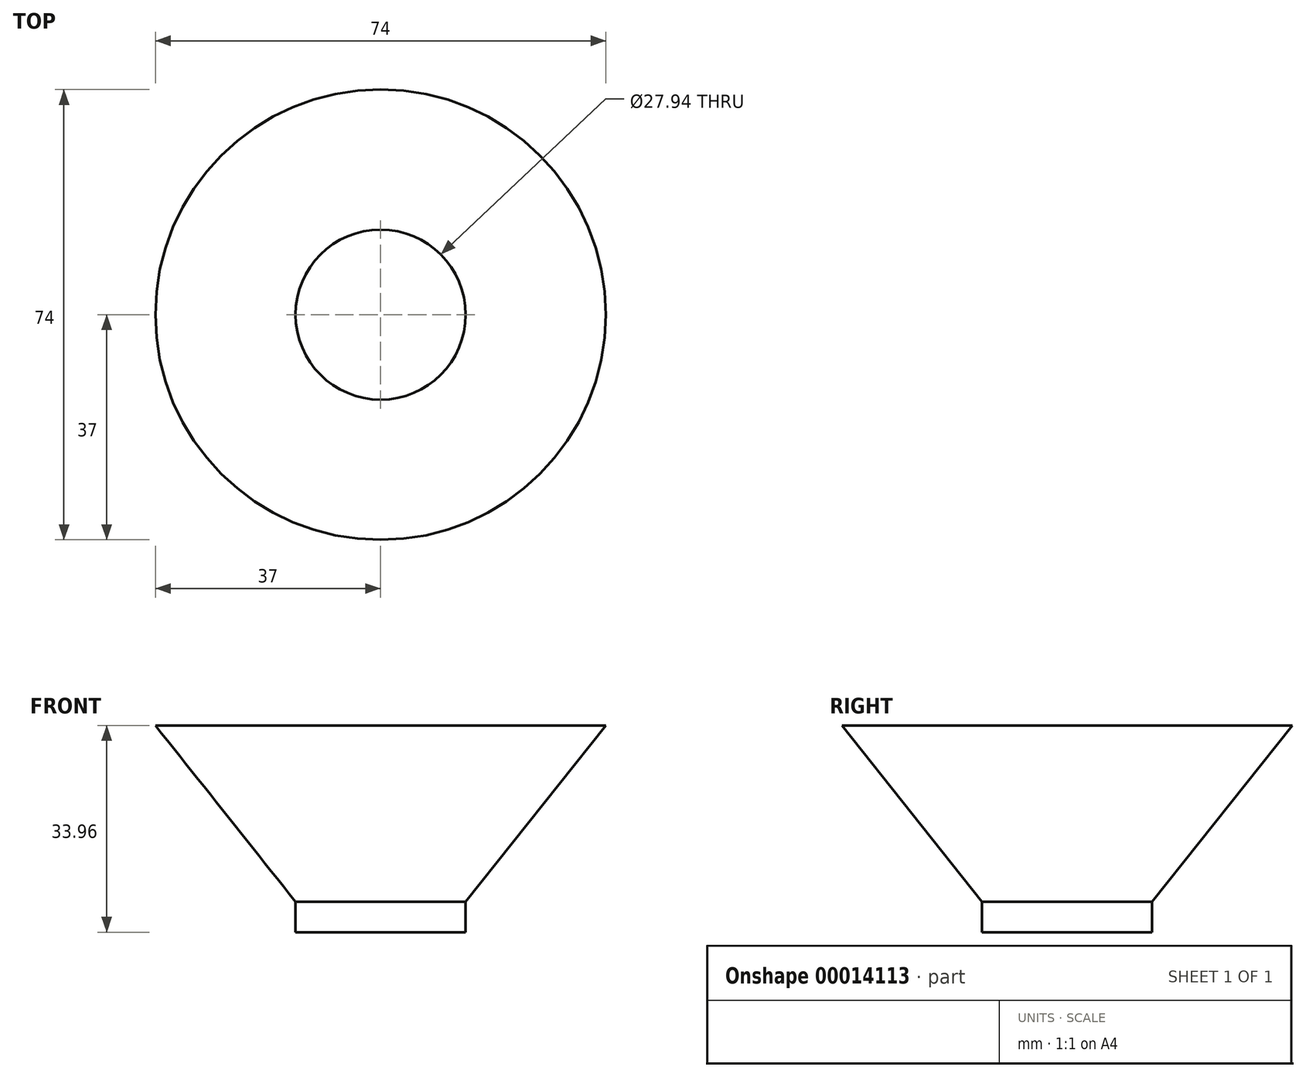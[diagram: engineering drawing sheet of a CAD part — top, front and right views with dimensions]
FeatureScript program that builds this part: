
annotation { "Feature Type Name" : "Feature", "Feature Type Description" : "" }
export const myFeature = defineFeature(function(context is Context, id is Id, definition is map)
    precondition{}
    {
        {
            var Q0;
            Q0=qCreatedBy(makeId("Front.planeOp"),FACE);
            var sketch = newSketch(context, id + "F0", { "sketchPlane" : qUnion([Q0])});
            skLineSegment(sketch, "E0", {"start": v(0, 121.53) * mm, "end": v(0, -120.25) * mm, "construction": true});
            skLineSegment(sketch, "E1", {"start": v(37, -90.97) * mm, "end": v(13.97, -119.93) * mm});
            skLineSegment(sketch, "E2", {"start": v(13.97, -119.93) * mm, "end": v(13.97, -129.93) * mm, "construction": true});
            skLineSegment(sketch, "E3", {"start": v(13.97, -119.93) * mm, "end": v(13.97, -124.93) * mm});
            skSolve(sketch);
        }
        {
            var Q0;
            Q0=sQuery(id+"F0.wireOp",EDGE,"E3");
            var Q1;
            Q1=sQuery(id+"F0.wireOp",EDGE,"E1");
            var Q2;
            Q2=sQuery(id+"F0.wireOp",EDGE,"E0");
            revolve(context, id + "F1", {"bodyType" : ToolBodyType.SURFACE, "surfaceEntities" : qUnion([Q0, Q1]), "axis" : qUnion([Q2]), "revolveType" : RevolveType.FULL});
        }
    });
